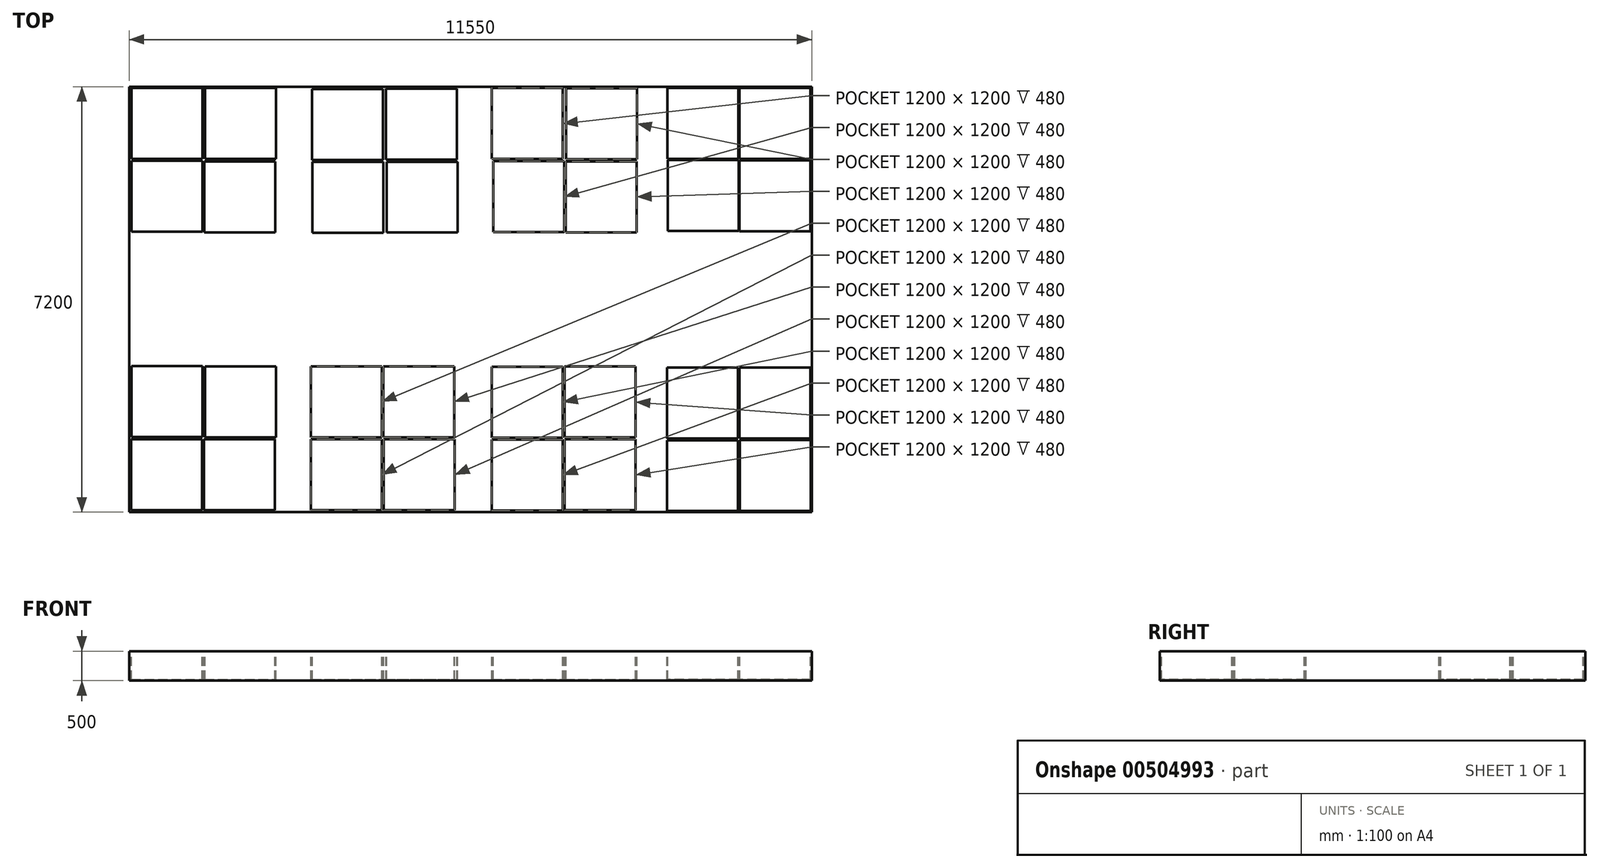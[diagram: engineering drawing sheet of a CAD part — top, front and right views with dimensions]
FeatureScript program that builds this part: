
annotation { "Feature Type Name" : "Feature", "Feature Type Description" : "" }
export const myFeature = defineFeature(function(context is Context, id is Id, definition is map)
    precondition{}
    {
        {
            var Q0;
            Q0=qCreatedBy(makeId("Top.planeOp"),FACE);
            var sketch = newSketch(context, id + "F0", { "sketchPlane" : qUnion([Q0])});
            skLineSegment(sketch, "E0.bottom", {"start": v(-4250.26, 2942.5) * mm, "end": v(7299.74, 2942.5) * mm});
            skLineSegment(sketch, "E0.top", {"start": v(-4250.26, -4257.5) * mm, "end": v(7299.74, -4257.5) * mm});
            skLineSegment(sketch, "E0.left", {"start": v(-4250.26, 2942.5) * mm, "end": v(-4250.26, -4257.5) * mm});
            skLineSegment(sketch, "E0.right", {"start": v(7299.74, 2942.5) * mm, "end": v(7299.74, -4257.5) * mm});
            skSolve(sketch);
        }
        {
            var Q0;
            Q0=makeQuery(id+"F0.imprint","IMPRINT",FACE,{"disambiguationData":[TD([[makeQuery(id+"F0.imprint","IMPRINT",EDGE,{"derivedFrom":sQuery(id+"F0.wireOp",EDGE,"E0.bottom")}),-1.0]])]});
            extrude(context, id + "F1", {"entities" : qUnion([Q0]), "oppositeDirection" : true, "depth" : 500 * mm});
        }
        {
            var Q0;
            Q0=qCreatedBy(makeId("Top.planeOp"),FACE);
            var sketch = newSketch(context, id + "F2", { "sketchPlane" : qUnion([Q0])});
            skLineSegment(sketch, "E1.bottom", {"start": v(-4210.09, 2918.5) * mm, "end": v(-3010.09, 2918.5) * mm});
            skLineSegment(sketch, "E1.top", {"start": v(-4210.09, 1718.5) * mm, "end": v(-3010.09, 1718.5) * mm});
            skLineSegment(sketch, "E1.left", {"start": v(-4210.09, 2918.5) * mm, "end": v(-4210.09, 1718.5) * mm});
            skLineSegment(sketch, "E1.right", {"start": v(-3010.09, 2918.5) * mm, "end": v(-3010.09, 1718.5) * mm});
            skSolve(sketch);
        }
        {
            var Q0;
            Q0 = qSketchRegion(id + "F2", true);
            extrude(context, id + "F3", {"entities" : qUnion([Q0]), "operationType" : NewBodyOperationType.REMOVE, "oppositeDirection" : true, "depth" : 480 * mm});
        }
        {
            var Q0;
            Q0=qCreatedBy(makeId("Top.planeOp"),FACE);
            var sketch = newSketch(context, id + "F4", { "sketchPlane" : qUnion([Q0])});
            skLineSegment(sketch, "E2.bottom", {"start": v(-2965.31, 2920.04) * mm, "end": v(-1765.31, 2920.04) * mm});
            skLineSegment(sketch, "E2.top", {"start": v(-2965.31, 1720.04) * mm, "end": v(-1765.31, 1720.04) * mm});
            skLineSegment(sketch, "E2.left", {"start": v(-2965.31, 2920.04) * mm, "end": v(-2965.31, 1720.04) * mm});
            skLineSegment(sketch, "E2.right", {"start": v(-1765.31, 2920.04) * mm, "end": v(-1765.31, 1720.04) * mm});
            skSolve(sketch);
        }
        {
            var Q0;
            Q0=makeQuery(id+"F4.imprint","IMPRINT",FACE,{"disambiguationData":[TD([[makeQuery(id+"F4.imprint","IMPRINT",EDGE,{"derivedFrom":sQuery(id+"F4.wireOp",EDGE,"E2.bottom")}),-1.0]])]});
            extrude(context, id + "F5", {"entities" : qUnion([Q0]), "operationType" : NewBodyOperationType.REMOVE, "oppositeDirection" : true, "depth" : 480 * mm});
        }
        {
            var Q0;
            Q0=qCreatedBy(makeId("Top.planeOp"),FACE);
            var sketch = newSketch(context, id + "F6", { "sketchPlane" : qUnion([Q0])});
            skLineSegment(sketch, "E3.bottom", {"start": v(-4210.1, 1685.9) * mm, "end": v(-3010.1, 1685.9) * mm});
            skLineSegment(sketch, "E3.top", {"start": v(-4210.1, 485.9) * mm, "end": v(-3010.1, 485.9) * mm});
            skLineSegment(sketch, "E3.left", {"start": v(-4210.1, 1685.9) * mm, "end": v(-4210.1, 485.9) * mm});
            skLineSegment(sketch, "E3.right", {"start": v(-3010.1, 1685.9) * mm, "end": v(-3010.1, 485.9) * mm});
            skSolve(sketch);
        }
        {
            var Q0;
            Q0=makeQuery(id+"F6.imprint","IMPRINT",FACE,{"disambiguationData":[TD([[makeQuery(id+"F6.imprint","IMPRINT",EDGE,{"derivedFrom":sQuery(id+"F6.wireOp",EDGE,"E3.bottom")}),-1.0]])]});
            extrude(context, id + "F7", {"entities" : qUnion([Q0]), "operationType" : NewBodyOperationType.REMOVE, "oppositeDirection" : true, "depth" : 480 * mm});
        }
        {
            var Q0;
            Q0=qCreatedBy(makeId("Top.planeOp"),FACE);
            var sketch = newSketch(context, id + "F8", { "sketchPlane" : qUnion([Q0])});
            skLineSegment(sketch, "E4.bottom", {"start": v(-2975.66, 1673.14) * mm, "end": v(-1775.66, 1673.14) * mm});
            skLineSegment(sketch, "E4.top", {"start": v(-2975.66, 473.14) * mm, "end": v(-1775.66, 473.14) * mm});
            skLineSegment(sketch, "E4.left", {"start": v(-2975.66, 1673.14) * mm, "end": v(-2975.66, 473.14) * mm});
            skLineSegment(sketch, "E4.right", {"start": v(-1775.66, 1673.14) * mm, "end": v(-1775.66, 473.14) * mm});
            skSolve(sketch);
        }
        {
            var Q0;
            Q0=makeQuery(id+"F8.imprint","IMPRINT",FACE,{"disambiguationData":[TD([[makeQuery(id+"F8.imprint","IMPRINT",EDGE,{"derivedFrom":sQuery(id+"F8.wireOp",EDGE,"E4.bottom")}),-1.0]])]});
            extrude(context, id + "F9", {"entities" : qUnion([Q0]), "operationType" : NewBodyOperationType.REMOVE, "oppositeDirection" : true, "depth" : 480 * mm});
        }
        {
            var Q0;
            Q0=qCreatedBy(makeId("Top.planeOp"),FACE);
            var sketch = newSketch(context, id + "F10", { "sketchPlane" : qUnion([Q0])});
            skLineSegment(sketch, "E5.bottom", {"start": v(-4218.7, -4225.4) * mm, "end": v(-3018.7, -4225.4) * mm});
            skLineSegment(sketch, "E5.top", {"start": v(-4218.7, -3025.4) * mm, "end": v(-3018.7, -3025.4) * mm});
            skLineSegment(sketch, "E5.left", {"start": v(-4218.7, -4225.4) * mm, "end": v(-4218.7, -3025.4) * mm});
            skLineSegment(sketch, "E5.right", {"start": v(-3018.7, -4225.4) * mm, "end": v(-3018.7, -3025.4) * mm});
            skSolve(sketch);
        }
        {
            var Q0;
            Q0=makeQuery(id+"F10.imprint","IMPRINT",FACE,{"disambiguationData":[TD([[makeQuery(id+"F10.imprint","IMPRINT",EDGE,{"derivedFrom":sQuery(id+"F10.wireOp",EDGE,"E5.bottom")}),1.0]])]});
            extrude(context, id + "F11", {"entities" : qUnion([Q0]), "operationType" : NewBodyOperationType.REMOVE, "oppositeDirection" : true, "depth" : 480 * mm});
        }
        {
            var Q0;
            Q0=qCreatedBy(makeId("Top.planeOp"),FACE);
            var sketch = newSketch(context, id + "F12", { "sketchPlane" : qUnion([Q0])});
            skLineSegment(sketch, "E6.bottom", {"start": v(-4211.34, -2982.62) * mm, "end": v(-3011.34, -2982.62) * mm});
            skLineSegment(sketch, "E6.top", {"start": v(-4211.34, -1782.62) * mm, "end": v(-3011.34, -1782.62) * mm});
            skLineSegment(sketch, "E6.left", {"start": v(-4211.34, -2982.62) * mm, "end": v(-4211.34, -1782.62) * mm});
            skLineSegment(sketch, "E6.right", {"start": v(-3011.34, -2982.62) * mm, "end": v(-3011.34, -1782.62) * mm});
            skSolve(sketch);
        }
        {
            var Q0;
            Q0=makeQuery(id+"F12.imprint","IMPRINT",FACE,{"disambiguationData":[TD([[makeQuery(id+"F12.imprint","IMPRINT",EDGE,{"derivedFrom":sQuery(id+"F12.wireOp",EDGE,"E6.bottom")}),1.0]])]});
            extrude(context, id + "F13", {"entities" : qUnion([Q0]), "operationType" : NewBodyOperationType.REMOVE, "oppositeDirection" : true, "depth" : 480 * mm});
        }
        {
            var Q0;
            Q0=qCreatedBy(makeId("Top.planeOp"),FACE);
            var sketch = newSketch(context, id + "F14", { "sketchPlane" : qUnion([Q0])});
            skLineSegment(sketch, "E7.bottom", {"start": v(-2967.78, -2989.59) * mm, "end": v(-1767.78, -2989.59) * mm});
            skLineSegment(sketch, "E7.top", {"start": v(-2967.78, -1789.59) * mm, "end": v(-1767.78, -1789.59) * mm});
            skLineSegment(sketch, "E7.left", {"start": v(-2967.78, -2989.59) * mm, "end": v(-2967.78, -1789.59) * mm});
            skLineSegment(sketch, "E7.right", {"start": v(-1767.78, -2989.59) * mm, "end": v(-1767.78, -1789.59) * mm});
            skSolve(sketch);
        }
        {
            var Q0;
            Q0=makeQuery(id+"F14.imprint","IMPRINT",FACE,{"disambiguationData":[TD([[makeQuery(id+"F14.imprint","IMPRINT",EDGE,{"derivedFrom":sQuery(id+"F14.wireOp",EDGE,"E7.bottom")}),1.0]])]});
            extrude(context, id + "F15", {"entities" : qUnion([Q0]), "operationType" : NewBodyOperationType.REMOVE, "oppositeDirection" : true, "depth" : 480 * mm});
        }
        {
            var Q0;
            Q0=qCreatedBy(makeId("Top.planeOp"),FACE);
            var sketch = newSketch(context, id + "F16", { "sketchPlane" : qUnion([Q0])});
            skLineSegment(sketch, "E8.bottom", {"start": v(-2982.5, -4225.66) * mm, "end": v(-1782.5, -4225.66) * mm});
            skLineSegment(sketch, "E8.top", {"start": v(-2982.5, -3025.66) * mm, "end": v(-1782.5, -3025.66) * mm});
            skLineSegment(sketch, "E8.left", {"start": v(-2982.5, -4225.66) * mm, "end": v(-2982.5, -3025.66) * mm});
            skLineSegment(sketch, "E8.right", {"start": v(-1782.5, -4225.66) * mm, "end": v(-1782.5, -3025.66) * mm});
            skSolve(sketch);
        }
        {
            var Q0;
            Q0=makeQuery(id+"F16.imprint","IMPRINT",FACE,{"disambiguationData":[TD([[makeQuery(id+"F16.imprint","IMPRINT",EDGE,{"derivedFrom":sQuery(id+"F16.wireOp",EDGE,"E8.bottom")}),1.0]])]});
            extrude(context, id + "F17", {"entities" : qUnion([Q0]), "operationType" : NewBodyOperationType.REMOVE, "oppositeDirection" : true, "depth" : 480 * mm});
        }
        {
            var Q0;
            Q0=qCreatedBy(makeId("Top.planeOp"),FACE);
            var sketch = newSketch(context, id + "F18", { "sketchPlane" : qUnion([Q0])});
            skLineSegment(sketch, "E9.bottom", {"start": v(7279.53, 2922.08) * mm, "end": v(6079.53, 2922.08) * mm});
            skLineSegment(sketch, "E9.top", {"start": v(7279.53, 1722.08) * mm, "end": v(6079.53, 1722.08) * mm});
            skLineSegment(sketch, "E9.left", {"start": v(7279.53, 2922.08) * mm, "end": v(7279.53, 1722.08) * mm});
            skLineSegment(sketch, "E9.right", {"start": v(6079.53, 2922.08) * mm, "end": v(6079.53, 1722.08) * mm});
            skSolve(sketch);
        }
        {
            var Q0;
            Q0=makeQuery(id+"F18.imprint","IMPRINT",FACE,{"disambiguationData":[TD([[makeQuery(id+"F18.imprint","IMPRINT",EDGE,{"derivedFrom":sQuery(id+"F18.wireOp",EDGE,"E9.bottom")}),1.0]])]});
            extrude(context, id + "F19", {"entities" : qUnion([Q0]), "operationType" : NewBodyOperationType.REMOVE, "oppositeDirection" : true, "depth" : 480 * mm});
        }
        {
            var Q0;
            Q0=qCreatedBy(makeId("Top.planeOp"),FACE);
            var sketch = newSketch(context, id + "F20", { "sketchPlane" : qUnion([Q0])});
            skLineSegment(sketch, "E10.bottom", {"start": v(6060.02, 2922.92) * mm, "end": v(4860.02, 2922.92) * mm});
            skLineSegment(sketch, "E10.top", {"start": v(6060.02, 1722.92) * mm, "end": v(4860.02, 1722.92) * mm});
            skLineSegment(sketch, "E10.left", {"start": v(6060.02, 2922.92) * mm, "end": v(6060.02, 1722.92) * mm});
            skLineSegment(sketch, "E10.right", {"start": v(4860.02, 2922.92) * mm, "end": v(4860.02, 1722.92) * mm});
            skSolve(sketch);
        }
        {
            var Q0;
            Q0=makeQuery(id+"F20.imprint","IMPRINT",FACE,{"disambiguationData":[TD([[makeQuery(id+"F20.imprint","IMPRINT",EDGE,{"derivedFrom":sQuery(id+"F20.wireOp",EDGE,"E10.bottom")}),1.0]])]});
            extrude(context, id + "F21", {"entities" : qUnion([Q0]), "operationType" : NewBodyOperationType.REMOVE, "oppositeDirection" : true, "depth" : 480 * mm});
        }
        {
            var Q0;
            Q0=qCreatedBy(makeId("Top.planeOp"),FACE);
            var sketch = newSketch(context, id + "F22", { "sketchPlane" : qUnion([Q0])});
            skLineSegment(sketch, "E11.bottom", {"start": v(4863.48, 1699.99) * mm, "end": v(6063.48, 1699.99) * mm});
            skLineSegment(sketch, "E11.top", {"start": v(4863.48, 499.99) * mm, "end": v(6063.48, 499.99) * mm});
            skLineSegment(sketch, "E11.left", {"start": v(4863.48, 1699.99) * mm, "end": v(4863.48, 499.99) * mm});
            skLineSegment(sketch, "E11.right", {"start": v(6063.48, 1699.99) * mm, "end": v(6063.48, 499.99) * mm});
            skSolve(sketch);
        }
        {
            var Q0;
            Q0=makeQuery(id+"F22.imprint","IMPRINT",FACE,{"disambiguationData":[TD([[makeQuery(id+"F22.imprint","IMPRINT",EDGE,{"derivedFrom":sQuery(id+"F22.wireOp",EDGE,"E11.bottom")}),-1.0]])]});
            extrude(context, id + "F23", {"entities" : qUnion([Q0]), "operationType" : NewBodyOperationType.REMOVE, "oppositeDirection" : true, "depth" : 480 * mm});
        }
        {
            var Q0;
            Q0=qCreatedBy(makeId("Top.planeOp"),FACE);
            var sketch = newSketch(context, id + "F24", { "sketchPlane" : qUnion([Q0])});
            skLineSegment(sketch, "E12.bottom", {"start": v(6079, 1697.62) * mm, "end": v(7279, 1697.62) * mm});
            skLineSegment(sketch, "E12.top", {"start": v(6079, 497.62) * mm, "end": v(7279, 497.62) * mm});
            skLineSegment(sketch, "E12.left", {"start": v(6079, 1697.62) * mm, "end": v(6079, 497.62) * mm});
            skLineSegment(sketch, "E12.right", {"start": v(7279, 1697.62) * mm, "end": v(7279, 497.62) * mm});
            skSolve(sketch);
        }
        {
            var Q0;
            Q0=makeQuery(id+"F24.imprint","IMPRINT",FACE,{"disambiguationData":[TD([[makeQuery(id+"F24.imprint","IMPRINT",EDGE,{"derivedFrom":sQuery(id+"F24.wireOp",EDGE,"E12.bottom")}),-1.0]])]});
            extrude(context, id + "F25", {"entities" : qUnion([Q0]), "operationType" : NewBodyOperationType.REMOVE, "oppositeDirection" : true, "depth" : 480 * mm});
        }
        {
            var Q0;
            Q0=qCreatedBy(makeId("Top.planeOp"),FACE);
            var sketch = newSketch(context, id + "F26", { "sketchPlane" : qUnion([Q0])});
            skLineSegment(sketch, "E13.bottom", {"start": v(7282, -4237.26) * mm, "end": v(6082, -4237.26) * mm});
            skLineSegment(sketch, "E13.top", {"start": v(7282, -3037.26) * mm, "end": v(6082, -3037.26) * mm});
            skLineSegment(sketch, "E13.left", {"start": v(7282, -4237.26) * mm, "end": v(7282, -3037.26) * mm});
            skLineSegment(sketch, "E13.right", {"start": v(6082, -4237.26) * mm, "end": v(6082, -3037.26) * mm});
            skSolve(sketch);
        }
        {
            var Q0;
            Q0=makeQuery(id+"F26.imprint","IMPRINT",FACE,{"disambiguationData":[TD([[makeQuery(id+"F26.imprint","IMPRINT",EDGE,{"derivedFrom":sQuery(id+"F26.wireOp",EDGE,"E13.bottom")}),-1.0]])]});
            extrude(context, id + "F27", {"entities" : qUnion([Q0]), "operationType" : NewBodyOperationType.REMOVE, "oppositeDirection" : true, "depth" : 480 * mm});
        }
        {
            var Q0;
            Q0=qCreatedBy(makeId("Top.planeOp"),FACE);
            var sketch = newSketch(context, id + "F28", { "sketchPlane" : qUnion([Q0])});
            skLineSegment(sketch, "E14.bottom", {"start": v(7279.8, -3010.01) * mm, "end": v(6079.8, -3010.01) * mm});
            skLineSegment(sketch, "E14.top", {"start": v(7279.8, -1810.01) * mm, "end": v(6079.8, -1810.01) * mm});
            skLineSegment(sketch, "E14.left", {"start": v(7279.8, -3010.01) * mm, "end": v(7279.8, -1810.01) * mm});
            skLineSegment(sketch, "E14.right", {"start": v(6079.8, -3010.01) * mm, "end": v(6079.8, -1810.01) * mm});
            skSolve(sketch);
        }
        {
            var Q0;
            Q0=makeQuery(id+"F28.imprint","IMPRINT",FACE,{"disambiguationData":[TD([[makeQuery(id+"F28.imprint","IMPRINT",EDGE,{"derivedFrom":sQuery(id+"F28.wireOp",EDGE,"E14.bottom")}),-1.0]])]});
            extrude(context, id + "F29", {"entities" : qUnion([Q0]), "operationType" : NewBodyOperationType.REMOVE, "oppositeDirection" : true, "depth" : 480 * mm});
        }
        {
            var Q0;
            Q0=qCreatedBy(makeId("Top.planeOp"),FACE);
            var sketch = newSketch(context, id + "F30", { "sketchPlane" : qUnion([Q0])});
            skLineSegment(sketch, "E15.bottom", {"start": v(6051.71, -3011.6) * mm, "end": v(4851.71, -3011.6) * mm});
            skLineSegment(sketch, "E15.top", {"start": v(6051.71, -1811.6) * mm, "end": v(4851.71, -1811.6) * mm});
            skLineSegment(sketch, "E15.left", {"start": v(6051.71, -3011.6) * mm, "end": v(6051.71, -1811.6) * mm});
            skLineSegment(sketch, "E15.right", {"start": v(4851.71, -3011.6) * mm, "end": v(4851.71, -1811.6) * mm});
            skSolve(sketch);
        }
        {
            var Q0;
            Q0=makeQuery(id+"F30.imprint","IMPRINT",FACE,{"disambiguationData":[TD([[makeQuery(id+"F30.imprint","IMPRINT",EDGE,{"derivedFrom":sQuery(id+"F30.wireOp",EDGE,"E15.bottom")}),-1.0]])]});
            extrude(context, id + "F31", {"entities" : qUnion([Q0]), "operationType" : NewBodyOperationType.REMOVE, "oppositeDirection" : true, "depth" : 480 * mm});
        }
        {
            var Q0;
            Q0=qCreatedBy(makeId("Top.planeOp"),FACE);
            var sketch = newSketch(context, id + "F32", { "sketchPlane" : qUnion([Q0])});
            skLineSegment(sketch, "E16.bottom", {"start": v(6050.86, -4238.86) * mm, "end": v(4850.86, -4238.86) * mm});
            skLineSegment(sketch, "E16.top", {"start": v(6050.86, -3038.86) * mm, "end": v(4850.86, -3038.86) * mm});
            skLineSegment(sketch, "E16.left", {"start": v(6050.86, -4238.86) * mm, "end": v(6050.86, -3038.86) * mm});
            skLineSegment(sketch, "E16.right", {"start": v(4850.86, -4238.86) * mm, "end": v(4850.86, -3038.86) * mm});
            skSolve(sketch);
        }
        {
            var Q0;
            Q0=makeQuery(id+"F32.imprint","IMPRINT",FACE,{"disambiguationData":[TD([[makeQuery(id+"F32.imprint","IMPRINT",EDGE,{"derivedFrom":sQuery(id+"F32.wireOp",EDGE,"E16.bottom")}),-1.0]])]});
            extrude(context, id + "F33", {"entities" : qUnion([Q0]), "operationType" : NewBodyOperationType.REMOVE, "oppositeDirection" : true, "depth" : 480 * mm});
        }
        {
            var Q0;
            Q0=qCreatedBy(makeId("Top.planeOp"),FACE);
            var sketch = newSketch(context, id + "F34", { "sketchPlane" : qUnion([Q0])});
            skLineSegment(sketch, "E17.bottom", {"start": v(-1153.72, 2904.11) * mm, "end": v(46.28, 2904.11) * mm});
            skLineSegment(sketch, "E17.top", {"start": v(-1153.72, 1704.11) * mm, "end": v(46.28, 1704.11) * mm});
            skLineSegment(sketch, "E17.left", {"start": v(-1153.72, 2904.11) * mm, "end": v(-1153.72, 1704.11) * mm});
            skLineSegment(sketch, "E17.right", {"start": v(46.28, 2904.11) * mm, "end": v(46.28, 1704.11) * mm});
            skSolve(sketch);
        }
        {
            var Q0;
            Q0=makeQuery(id+"F34.imprint","IMPRINT",FACE,{"disambiguationData":[TD([[makeQuery(id+"F34.imprint","IMPRINT",EDGE,{"derivedFrom":sQuery(id+"F34.wireOp",EDGE,"E17.bottom")}),-1.0]])]});
            extrude(context, id + "F35", {"entities" : qUnion([Q0]), "operationType" : NewBodyOperationType.REMOVE, "oppositeDirection" : true, "depth" : 480 * mm});
        }
        {
            var Q0;
            Q0=qCreatedBy(makeId("Top.planeOp"),FACE);
            var sketch = newSketch(context, id + "F36", { "sketchPlane" : qUnion([Q0])});
            skLineSegment(sketch, "E18.bottom", {"start": v(-1146.18, 1666.73) * mm, "end": v(53.82, 1666.73) * mm});
            skLineSegment(sketch, "E18.top", {"start": v(-1146.18, 466.73) * mm, "end": v(53.82, 466.73) * mm});
            skLineSegment(sketch, "E18.left", {"start": v(-1146.18, 1666.73) * mm, "end": v(-1146.18, 466.73) * mm});
            skLineSegment(sketch, "E18.right", {"start": v(53.82, 1666.73) * mm, "end": v(53.82, 466.73) * mm});
            skSolve(sketch);
        }
        {
            var Q0;
            Q0=makeQuery(id+"F36.imprint","IMPRINT",FACE,{"disambiguationData":[TD([[makeQuery(id+"F36.imprint","IMPRINT",EDGE,{"derivedFrom":sQuery(id+"F36.wireOp",EDGE,"E18.bottom")}),-1.0]])]});
            extrude(context, id + "F37", {"entities" : qUnion([Q0]), "operationType" : NewBodyOperationType.REMOVE, "oppositeDirection" : true, "depth" : 480 * mm});
        }
        {
            var Q0;
            Q0=qCreatedBy(makeId("Top.planeOp"),FACE);
            var sketch = newSketch(context, id + "F38", { "sketchPlane" : qUnion([Q0])});
            skLineSegment(sketch, "E19.bottom", {"start": v(106.12, 1672.95) * mm, "end": v(1306.12, 1672.95) * mm});
            skLineSegment(sketch, "E19.top", {"start": v(106.12, 472.95) * mm, "end": v(1306.12, 472.95) * mm});
            skLineSegment(sketch, "E19.left", {"start": v(106.12, 1672.95) * mm, "end": v(106.12, 472.95) * mm});
            skLineSegment(sketch, "E19.right", {"start": v(1306.12, 1672.95) * mm, "end": v(1306.12, 472.95) * mm});
            skSolve(sketch);
        }
        {
            var Q0;
            Q0=makeQuery(id+"F38.imprint","IMPRINT",FACE,{"disambiguationData":[TD([[makeQuery(id+"F38.imprint","IMPRINT",EDGE,{"derivedFrom":sQuery(id+"F38.wireOp",EDGE,"E19.bottom")}),-1.0]])]});
            extrude(context, id + "F39", {"entities" : qUnion([Q0]), "operationType" : NewBodyOperationType.REMOVE, "oppositeDirection" : true, "depth" : 480 * mm});
        }
        {
            var Q0;
            Q0=qCreatedBy(makeId("Top.planeOp"),FACE);
            var sketch = newSketch(context, id + "F40", { "sketchPlane" : qUnion([Q0])});
            skLineSegment(sketch, "E20.bottom", {"start": v(98.44, 2905.22) * mm, "end": v(1298.44, 2905.22) * mm});
            skLineSegment(sketch, "E20.top", {"start": v(98.44, 1705.22) * mm, "end": v(1298.44, 1705.22) * mm});
            skLineSegment(sketch, "E20.left", {"start": v(98.44, 2905.22) * mm, "end": v(98.44, 1705.22) * mm});
            skLineSegment(sketch, "E20.right", {"start": v(1298.44, 2905.22) * mm, "end": v(1298.44, 1705.22) * mm});
            skSolve(sketch);
        }
        {
            var Q0;
            Q0=makeQuery(id+"F40.imprint","IMPRINT",FACE,{"disambiguationData":[TD([[makeQuery(id+"F40.imprint","IMPRINT",EDGE,{"derivedFrom":sQuery(id+"F40.wireOp",EDGE,"E20.bottom")}),-1.0]])]});
            extrude(context, id + "F41", {"entities" : qUnion([Q0]), "operationType" : NewBodyOperationType.REMOVE, "oppositeDirection" : true, "depth" : 480 * mm});
        }
        {
            var Q0;
            Q0=qCreatedBy(makeId("Top.planeOp"),FACE);
            var sketch = newSketch(context, id + "F42", { "sketchPlane" : qUnion([Q0])});
            skLineSegment(sketch, "E21.bottom", {"start": v(1888.66, 2920.3) * mm, "end": v(3088.66, 2920.3) * mm});
            skLineSegment(sketch, "E21.top", {"start": v(1888.66, 1720.3) * mm, "end": v(3088.66, 1720.3) * mm});
            skLineSegment(sketch, "E21.left", {"start": v(1888.66, 2920.3) * mm, "end": v(1888.66, 1720.3) * mm});
            skLineSegment(sketch, "E21.right", {"start": v(3088.66, 2920.3) * mm, "end": v(3088.66, 1720.3) * mm});
            skSolve(sketch);
        }
        {
            var Q0;
            Q0=makeQuery(id+"F42.imprint","IMPRINT",FACE,{"disambiguationData":[TD([[makeQuery(id+"F42.imprint","IMPRINT",EDGE,{"derivedFrom":sQuery(id+"F42.wireOp",EDGE,"E21.bottom")}),-1.0]])]});
            extrude(context, id + "F43", {"entities" : qUnion([Q0]), "operationType" : NewBodyOperationType.REMOVE, "oppositeDirection" : true, "depth" : 480 * mm});
        }
        {
            var Q0;
            Q0=qCreatedBy(makeId("Top.planeOp"),FACE);
            var sketch = newSketch(context, id + "F44", { "sketchPlane" : qUnion([Q0])});
            skLineSegment(sketch, "E22.bottom", {"start": v(1909.4, 1681.33) * mm, "end": v(3109.4, 1681.33) * mm});
            skLineSegment(sketch, "E22.top", {"start": v(1909.4, 481.33) * mm, "end": v(3109.4, 481.33) * mm});
            skLineSegment(sketch, "E22.left", {"start": v(1909.4, 1681.33) * mm, "end": v(1909.4, 481.33) * mm});
            skLineSegment(sketch, "E22.right", {"start": v(3109.4, 1681.33) * mm, "end": v(3109.4, 481.33) * mm});
            skSolve(sketch);
        }
        {
            var Q0;
            Q0=makeQuery(id+"F44.imprint","IMPRINT",FACE,{"disambiguationData":[TD([[makeQuery(id+"F44.imprint","IMPRINT",EDGE,{"derivedFrom":sQuery(id+"F44.wireOp",EDGE,"E22.bottom")}),-1.0]])]});
            extrude(context, id + "F45", {"entities" : qUnion([Q0]), "operationType" : NewBodyOperationType.REMOVE, "oppositeDirection" : true, "depth" : 480 * mm});
        }
        {
            var Q0;
            Q0=qCreatedBy(makeId("Top.planeOp"),FACE);
            var sketch = newSketch(context, id + "F46", { "sketchPlane" : qUnion([Q0])});
            skLineSegment(sketch, "E23.bottom", {"start": v(3140.82, 2915.97) * mm, "end": v(4340.82, 2915.97) * mm});
            skLineSegment(sketch, "E23.top", {"start": v(3140.82, 1715.97) * mm, "end": v(4340.82, 1715.97) * mm});
            skLineSegment(sketch, "E23.left", {"start": v(3140.82, 2915.97) * mm, "end": v(3140.82, 1715.97) * mm});
            skLineSegment(sketch, "E23.right", {"start": v(4340.82, 2915.97) * mm, "end": v(4340.82, 1715.97) * mm});
            skSolve(sketch);
        }
        {
            var Q0;
            Q0=makeQuery(id+"F46.imprint","IMPRINT",FACE,{"disambiguationData":[TD([[makeQuery(id+"F46.imprint","IMPRINT",EDGE,{"derivedFrom":sQuery(id+"F46.wireOp",EDGE,"E23.bottom")}),-1.0]])]});
            extrude(context, id + "F47", {"entities" : qUnion([Q0]), "operationType" : NewBodyOperationType.REMOVE, "oppositeDirection" : true, "depth" : 480 * mm});
        }
        {
            var Q0;
            Q0=qCreatedBy(makeId("Top.planeOp"),FACE);
            var sketch = newSketch(context, id + "F48", { "sketchPlane" : qUnion([Q0])});
            skLineSegment(sketch, "E24.bottom", {"start": v(3139.92, 1677.04) * mm, "end": v(4339.92, 1677.04) * mm});
            skLineSegment(sketch, "E24.top", {"start": v(3139.92, 477.04) * mm, "end": v(4339.92, 477.04) * mm});
            skLineSegment(sketch, "E24.left", {"start": v(3139.92, 1677.04) * mm, "end": v(3139.92, 477.04) * mm});
            skLineSegment(sketch, "E24.right", {"start": v(4339.92, 1677.04) * mm, "end": v(4339.92, 477.04) * mm});
            skSolve(sketch);
        }
        {
            var Q0;
            Q0=makeQuery(id+"F48.imprint","IMPRINT",FACE,{"disambiguationData":[TD([[makeQuery(id+"F48.imprint","IMPRINT",EDGE,{"derivedFrom":sQuery(id+"F48.wireOp",EDGE,"E24.bottom")}),-1.0]])]});
            extrude(context, id + "F49", {"entities" : qUnion([Q0]), "operationType" : NewBodyOperationType.REMOVE, "oppositeDirection" : true, "depth" : 480 * mm});
        }
        {
            var Q0;
            Q0=qCreatedBy(makeId("Top.planeOp"),FACE);
            var sketch = newSketch(context, id + "F50", { "sketchPlane" : qUnion([Q0])});
            skLineSegment(sketch, "E25.bottom", {"start": v(-1176.65, -1790.05) * mm, "end": v(23.35, -1790.05) * mm});
            skLineSegment(sketch, "E25.top", {"start": v(-1176.65, -2990.05) * mm, "end": v(23.35, -2990.05) * mm});
            skLineSegment(sketch, "E25.left", {"start": v(-1176.65, -1790.05) * mm, "end": v(-1176.65, -2990.05) * mm});
            skLineSegment(sketch, "E25.right", {"start": v(23.35, -1790.05) * mm, "end": v(23.35, -2990.05) * mm});
            skSolve(sketch);
        }
        {
            var Q0;
            Q0=makeQuery(id+"F50.imprint","IMPRINT",FACE,{"disambiguationData":[TD([[makeQuery(id+"F50.imprint","IMPRINT",EDGE,{"derivedFrom":sQuery(id+"F50.wireOp",EDGE,"E25.bottom")}),-1.0]])]});
            extrude(context, id + "F51", {"entities" : qUnion([Q0]), "operationType" : NewBodyOperationType.REMOVE, "oppositeDirection" : true, "depth" : 480 * mm});
        }
        {
            var Q0;
            Q0=qCreatedBy(makeId("Top.planeOp"),FACE);
            var sketch = newSketch(context, id + "F52", { "sketchPlane" : qUnion([Q0])});
            skLineSegment(sketch, "E26.bottom", {"start": v(-1177.33, -3023.25) * mm, "end": v(22.67, -3023.25) * mm});
            skLineSegment(sketch, "E26.top", {"start": v(-1177.33, -4223.25) * mm, "end": v(22.67, -4223.25) * mm});
            skLineSegment(sketch, "E26.left", {"start": v(-1177.33, -3023.25) * mm, "end": v(-1177.33, -4223.25) * mm});
            skLineSegment(sketch, "E26.right", {"start": v(22.67, -3023.25) * mm, "end": v(22.67, -4223.25) * mm});
            skSolve(sketch);
        }
        {
            var Q0;
            Q0=makeQuery(id+"F52.imprint","IMPRINT",FACE,{"disambiguationData":[TD([[makeQuery(id+"F52.imprint","IMPRINT",EDGE,{"derivedFrom":sQuery(id+"F52.wireOp",EDGE,"E26.bottom")}),-1.0]])]});
            extrude(context, id + "F53", {"entities" : qUnion([Q0]), "operationType" : NewBodyOperationType.REMOVE, "oppositeDirection" : true, "depth" : 480 * mm});
        }
        {
            var Q0;
            Q0=qCreatedBy(makeId("Top.planeOp"),FACE);
            var sketch = newSketch(context, id + "F54", { "sketchPlane" : qUnion([Q0])});
            skLineSegment(sketch, "E27.bottom", {"start": v(49.51, -1788.82) * mm, "end": v(1249.51, -1788.82) * mm});
            skLineSegment(sketch, "E27.top", {"start": v(49.51, -2988.82) * mm, "end": v(1249.51, -2988.82) * mm});
            skLineSegment(sketch, "E27.left", {"start": v(49.51, -1788.82) * mm, "end": v(49.51, -2988.82) * mm});
            skLineSegment(sketch, "E27.right", {"start": v(1249.51, -1788.82) * mm, "end": v(1249.51, -2988.82) * mm});
            skSolve(sketch);
        }
        {
            var Q0;
            Q0=makeQuery(id+"F54.imprint","IMPRINT",FACE,{"disambiguationData":[TD([[makeQuery(id+"F54.imprint","IMPRINT",EDGE,{"derivedFrom":sQuery(id+"F54.wireOp",EDGE,"E27.bottom")}),-1.0]])]});
            extrude(context, id + "F55", {"entities" : qUnion([Q0]), "operationType" : NewBodyOperationType.REMOVE, "oppositeDirection" : true, "depth" : 480 * mm});
        }
        {
            var Q0;
            Q0=qCreatedBy(makeId("Top.planeOp"),FACE);
            var sketch = newSketch(context, id + "F56", { "sketchPlane" : qUnion([Q0])});
            skLineSegment(sketch, "E28.bottom", {"start": v(58.51, -3024.74) * mm, "end": v(1258.51, -3024.74) * mm});
            skLineSegment(sketch, "E28.top", {"start": v(58.51, -4224.74) * mm, "end": v(1258.51, -4224.74) * mm});
            skLineSegment(sketch, "E28.left", {"start": v(58.51, -3024.74) * mm, "end": v(58.51, -4224.74) * mm});
            skLineSegment(sketch, "E28.right", {"start": v(1258.51, -3024.74) * mm, "end": v(1258.51, -4224.74) * mm});
            skSolve(sketch);
        }
        {
            var Q0;
            Q0=makeQuery(id+"F56.imprint","IMPRINT",FACE,{"disambiguationData":[TD([[makeQuery(id+"F56.imprint","IMPRINT",EDGE,{"derivedFrom":sQuery(id+"F56.wireOp",EDGE,"E28.bottom")}),-1.0]])]});
            extrude(context, id + "F57", {"entities" : qUnion([Q0]), "operationType" : NewBodyOperationType.REMOVE, "oppositeDirection" : true, "depth" : 480 * mm});
        }
        {
            var Q0;
            Q0=qCreatedBy(makeId("Top.planeOp"),FACE);
            var sketch = newSketch(context, id + "F58", { "sketchPlane" : qUnion([Q0])});
            skLineSegment(sketch, "E29.bottom", {"start": v(1887.6, -1795.86) * mm, "end": v(3087.6, -1795.86) * mm});
            skLineSegment(sketch, "E29.top", {"start": v(1887.6, -2995.86) * mm, "end": v(3087.6, -2995.86) * mm});
            skLineSegment(sketch, "E29.left", {"start": v(1887.6, -1795.86) * mm, "end": v(1887.6, -2995.86) * mm});
            skLineSegment(sketch, "E29.right", {"start": v(3087.6, -1795.86) * mm, "end": v(3087.6, -2995.86) * mm});
            skSolve(sketch);
        }
        {
            var Q0;
            Q0=makeQuery(id+"F58.imprint","IMPRINT",FACE,{"disambiguationData":[TD([[makeQuery(id+"F58.imprint","IMPRINT",EDGE,{"derivedFrom":sQuery(id+"F58.wireOp",EDGE,"E29.bottom")}),-1.0]])]});
            extrude(context, id + "F59", {"entities" : qUnion([Q0]), "operationType" : NewBodyOperationType.REMOVE, "oppositeDirection" : true, "depth" : 480 * mm});
        }
        {
            var Q0;
            Q0=qCreatedBy(makeId("Top.planeOp"),FACE);
            var sketch = newSketch(context, id + "F60", { "sketchPlane" : qUnion([Q0])});
            skLineSegment(sketch, "E30.bottom", {"start": v(1888.06, -3027.82) * mm, "end": v(3088.06, -3027.82) * mm});
            skLineSegment(sketch, "E30.top", {"start": v(1888.06, -4227.82) * mm, "end": v(3088.06, -4227.82) * mm});
            skLineSegment(sketch, "E30.left", {"start": v(1888.06, -3027.82) * mm, "end": v(1888.06, -4227.82) * mm});
            skLineSegment(sketch, "E30.right", {"start": v(3088.06, -3027.82) * mm, "end": v(3088.06, -4227.82) * mm});
            skSolve(sketch);
        }
        {
            var Q0;
            Q0=makeQuery(id+"F60.imprint","IMPRINT",FACE,{"disambiguationData":[TD([[makeQuery(id+"F60.imprint","IMPRINT",EDGE,{"derivedFrom":sQuery(id+"F60.wireOp",EDGE,"E30.bottom")}),-1.0]])]});
            extrude(context, id + "F61", {"entities" : qUnion([Q0]), "operationType" : NewBodyOperationType.REMOVE, "oppositeDirection" : true, "depth" : 480 * mm});
        }
        {
            var Q0;
            Q0=qCreatedBy(makeId("Top.planeOp"),FACE);
            var sketch = newSketch(context, id + "F62", { "sketchPlane" : qUnion([Q0])});
            skLineSegment(sketch, "E31.bottom", {"start": v(3116.93, -1791.62) * mm, "end": v(4316.93, -1791.62) * mm});
            skLineSegment(sketch, "E31.top", {"start": v(3116.93, -2991.62) * mm, "end": v(4316.93, -2991.62) * mm});
            skLineSegment(sketch, "E31.left", {"start": v(3116.93, -1791.62) * mm, "end": v(3116.93, -2991.62) * mm});
            skLineSegment(sketch, "E31.right", {"start": v(4316.93, -1791.62) * mm, "end": v(4316.93, -2991.62) * mm});
            skSolve(sketch);
        }
        {
            var Q0;
            Q0=makeQuery(id+"F62.imprint","IMPRINT",FACE,{"disambiguationData":[TD([[makeQuery(id+"F62.imprint","IMPRINT",EDGE,{"derivedFrom":sQuery(id+"F62.wireOp",EDGE,"E31.bottom")}),-1.0]])]});
            extrude(context, id + "F63", {"entities" : qUnion([Q0]), "operationType" : NewBodyOperationType.REMOVE, "oppositeDirection" : true, "depth" : 480 * mm});
        }
        {
            var Q0;
            Q0=qCreatedBy(makeId("Top.planeOp"),FACE);
            var sketch = newSketch(context, id + "F64", { "sketchPlane" : qUnion([Q0])});
            skLineSegment(sketch, "E32.bottom", {"start": v(3120.4, -3025.57) * mm, "end": v(4320.4, -3025.57) * mm});
            skLineSegment(sketch, "E32.top", {"start": v(3120.4, -4225.57) * mm, "end": v(4320.4, -4225.57) * mm});
            skLineSegment(sketch, "E32.left", {"start": v(3120.4, -3025.57) * mm, "end": v(3120.4, -4225.57) * mm});
            skLineSegment(sketch, "E32.right", {"start": v(4320.4, -3025.57) * mm, "end": v(4320.4, -4225.57) * mm});
            skSolve(sketch);
        }
        {
            var Q0;
            Q0=makeQuery(id+"F64.imprint","IMPRINT",FACE,{"disambiguationData":[TD([[makeQuery(id+"F64.imprint","IMPRINT",EDGE,{"derivedFrom":sQuery(id+"F64.wireOp",EDGE,"E32.bottom")}),-1.0]])]});
            extrude(context, id + "F65", {"entities" : qUnion([Q0]), "operationType" : NewBodyOperationType.REMOVE, "oppositeDirection" : true, "depth" : 480 * mm});
        }
    });
